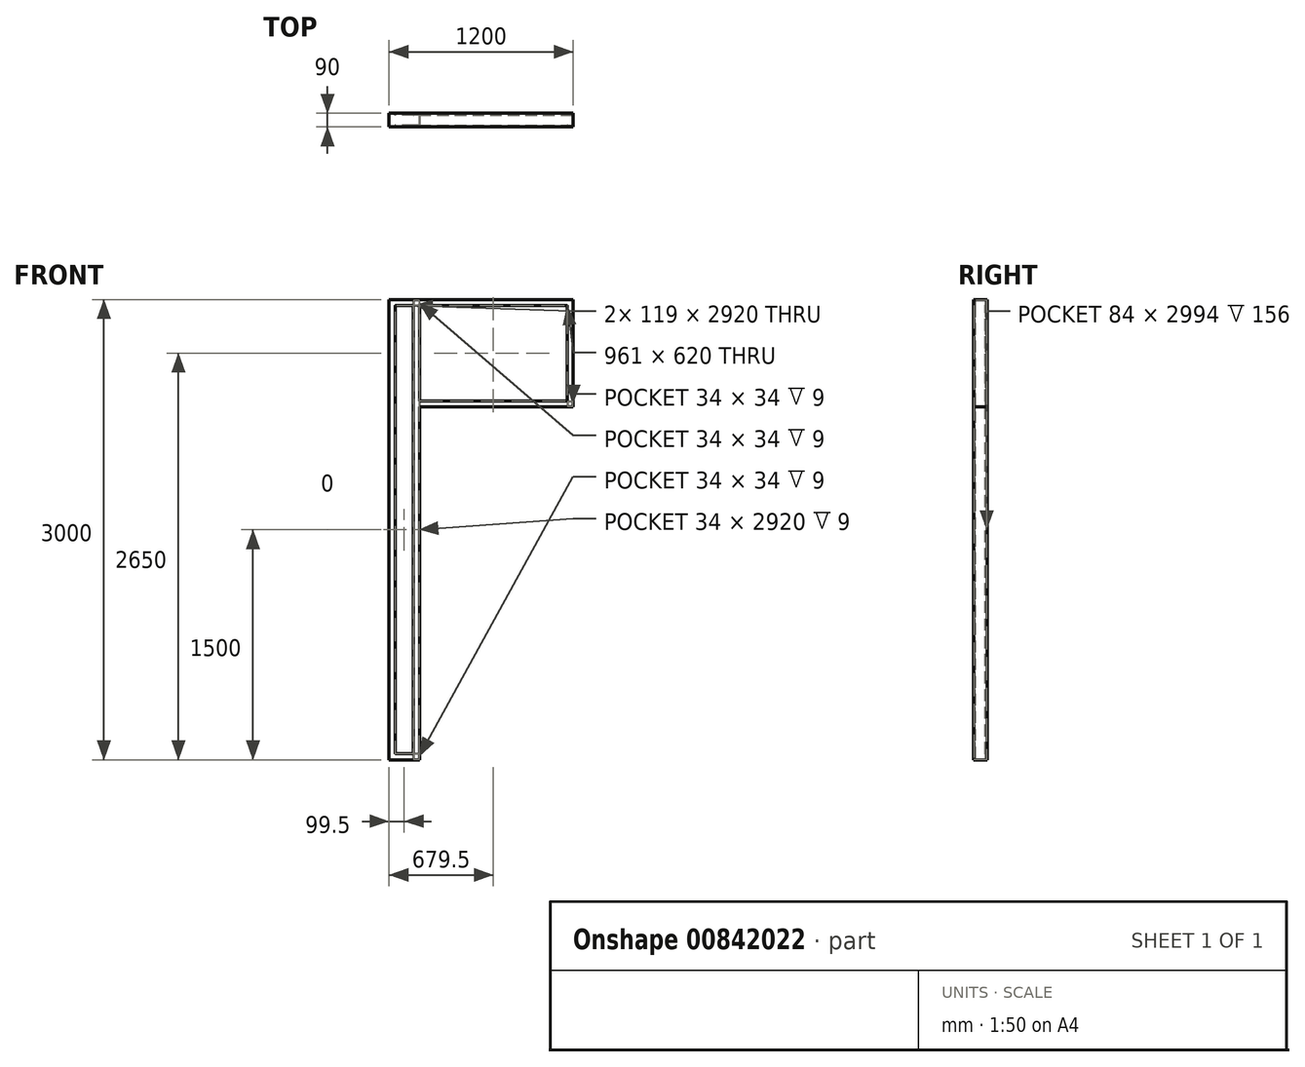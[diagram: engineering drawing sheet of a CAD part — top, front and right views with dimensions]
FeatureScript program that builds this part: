
annotation { "Feature Type Name" : "Feature", "Feature Type Description" : "" }
export const myFeature = defineFeature(function(context is Context, id is Id, definition is map)
    precondition{}
    {
        {
            var Q0;
            Q0=qCreatedBy(makeId("Front.planeOp"),FACE);
            var sketch = newSketch(context, id + "F0", { "sketchPlane" : qUnion([Q0])});
            skLineSegment(sketch, "E0.bottom", {"start": v(0, 0) * mm, "end": v(1200, 0) * mm});
            skLineSegment(sketch, "E0.top", {"start": v(0, 3000) * mm, "end": v(1200, 3000) * mm});
            skLineSegment(sketch, "E0.left", {"start": v(0, 0) * mm, "end": v(0, 3000) * mm});
            skLineSegment(sketch, "E0.right", {"start": v(1200, 0) * mm, "end": v(1200, 3000) * mm});
            skSolve(sketch);
        }
        {
            var Q0;
            Q0=qCreatedBy(makeId("Top.planeOp"),FACE);
            var sketch = newSketch(context, id + "F1", { "sketchPlane" : qUnion([Q0])});
            skLineSegment(sketch, "E1", {"start": v(0, 0) * mm, "end": v(0, -45) * mm});
            skLineSegment(sketch, "E2", {"start": v(0, -45) * mm, "end": v(40, -45) * mm});
            skLineSegment(sketch, "E3", {"start": v(40, -45) * mm, "end": v(40, -33) * mm});
            skLineSegment(sketch, "E4.MirrorCS", {"start": v(0, 0) * mm, "end": v(0, 45) * mm});
            skLineSegment(sketch, "E5.MirrorCS", {"start": v(0, 45) * mm, "end": v(40, 45) * mm});
            skLineSegment(sketch, "E6.MirrorCS", {"start": v(40, 45) * mm, "end": v(40, 33) * mm});
            skLineSegment(sketch, "E7.0", {"start": v(37, 42) * mm, "end": v(37, 33) * mm});
            skLineSegment(sketch, "E7.1", {"start": v(3, 42) * mm, "end": v(37, 42) * mm});
            skLineSegment(sketch, "E7.2", {"start": v(37, -42) * mm, "end": v(37, -33) * mm});
            skLineSegment(sketch, "E7.3", {"start": v(3, -42) * mm, "end": v(37, -42) * mm});
            skLineSegment(sketch, "E7.4", {"start": v(3, 0) * mm, "end": v(3, -42) * mm});
            skLineSegment(sketch, "E7.5", {"start": v(3, 0) * mm, "end": v(3, 42) * mm});
            skLineSegment(sketch, "E8", {"start": v(37, 33) * mm, "end": v(40, 33) * mm});
            skLineSegment(sketch, "E9", {"start": v(37, -33) * mm, "end": v(40, -33) * mm});
            skSolve(sketch);
        }
        {
            var Q0;
            Q0=qSketchRegion(id+"F1",true);
            var Q1;
            Q1=qConstructionFilter(qBodyType(qCreatedBy(id+"F0",EDGE),BodyType.WIRE),ConstructionObject.NO);
            sweep(context, id + "F2", {"profiles" : qUnion([Q0]), "path" : qUnion([Q1])});
        }
        {
            var Q0;
            Q0=qCreatedBy(makeId("Top.planeOp"),FACE);
            var sketch = newSketch(context, id + "F3", { "sketchPlane" : qUnion([Q0])});
            skLineSegment(sketch, "E10", {"start": v(159, -45) * mm, "end": v(199, -45) * mm});
            skLineSegment(sketch, "E11", {"start": v(199, -45) * mm, "end": v(199, 45) * mm});
            skLineSegment(sketch, "E12", {"start": v(199, 45) * mm, "end": v(159, 45) * mm});
            skLineSegment(sketch, "E13", {"start": v(159, 45) * mm, "end": v(159, 33) * mm});
            skLineSegment(sketch, "E14", {"start": v(159, -45) * mm, "end": v(159, -33) * mm});
            skLineSegment(sketch, "E15", {"start": v(200, -276.13) * mm, "end": v(200, 155.47) * mm, "construction": true});
            skLineSegment(sketch, "E16.0", {"start": v(1195, -40) * mm, "end": v(5, -40) * mm});
            skLineSegment(sketch, "E16.1", {"start": v(1195, 40) * mm, "end": v(1195, -40) * mm});
            skLineSegment(sketch, "E16.2", {"start": v(5, 40) * mm, "end": v(1195, 40) * mm});
            skLineSegment(sketch, "E16.3", {"start": v(5, 40) * mm, "end": v(5, -40) * mm});
            skLineSegment(sketch, "E17.0", {"start": v(162, 42) * mm, "end": v(162, 33) * mm});
            skLineSegment(sketch, "E17.1", {"start": v(162, -42) * mm, "end": v(162, -33) * mm});
            skLineSegment(sketch, "E17.2", {"start": v(162, -42) * mm, "end": v(196, -42) * mm});
            skLineSegment(sketch, "E17.3", {"start": v(196, -42) * mm, "end": v(196, 42) * mm});
            skLineSegment(sketch, "E17.4", {"start": v(196, 42) * mm, "end": v(162, 42) * mm});
            skLineSegment(sketch, "E18", {"start": v(162, -33) * mm, "end": v(159, -33) * mm});
            skLineSegment(sketch, "E19", {"start": v(162, 33) * mm, "end": v(159, 33) * mm});
            skSolve(sketch);
        }
        {
            var Q0;
            {var subQ1=sQuery(id+"F3.wireOp",EDGE,"E10");Q0=makeQuery(id+"F3.imprint","IMPRINT",FACE,{"disambiguationData":[TD([[makeQuery(id+"F3.imprint","IMPRINT",EDGE,{"derivedFrom":subQ1}),1.0]])]});}
            var Q1;
            {var subQ0=sQuery(id+"F3.wireOp",EDGE,"E16.0");var subQ1=sQuery(id+"F3.wireOp",EDGE,"E11");var subQ2=makeQuery(id+"F3.imprint","INTERSECT",VERTEX,{"derivedFrom":[subQ1,subQ0]});Q1=makeQuery(id+"F3.imprint","IMPRINT",FACE,{"disambiguationData":[TD([[makeQuery(id+"F3.imprint","IMPRINT",EDGE,{"disambiguationData":[TD([[subQ2,-1.0]])],"derivedFrom":subQ1}),1.0]])]});}
            var Q2;
            {var subQ0=sQuery(id+"F3.wireOp",EDGE,"E18");Q2=makeQuery(id+"F3.imprint","IMPRINT",FACE,{"disambiguationData":[TD([[makeQuery(id+"F3.imprint","IMPRINT",EDGE,{"derivedFrom":subQ0}),1.0]])]});}
            var Q3;
            {var subQ1=sQuery(id+"F3.wireOp",EDGE,"E12");Q3=makeQuery(id+"F3.imprint","IMPRINT",FACE,{"disambiguationData":[TD([[makeQuery(id+"F3.imprint","IMPRINT",EDGE,{"derivedFrom":subQ1}),1.0]])]});}
            var Q4;
            {var subQ0=sQuery(id+"F3.wireOp",EDGE,"E19");Q4=makeQuery(id+"F3.imprint","IMPRINT",FACE,{"disambiguationData":[TD([[makeQuery(id+"F3.imprint","IMPRINT",EDGE,{"derivedFrom":subQ0}),-1.0]])]});}
            var Q5;
            {var subQ0=sQuery(id+"F3.wireOp",EDGE,"fbeb7f0c-a459-400f-91ed-7fec257c8f050.MirrorCS");Q5=makeQuery(id+"F3.imprint","IMPRINT",FACE,{"disambiguationData":[TD([[makeQuery(id+"F3.imprint","IMPRINT",EDGE,{"derivedFrom":subQ0}),1.0]])]});}
            var Q6;
            {var subQ1=sQuery(id+"F3.wireOp",EDGE,"567eaf2c-da89-443f-b3b3-d68592a5250c0.MirrorCS");Q6=makeQuery(id+"F3.imprint","IMPRINT",FACE,{"disambiguationData":[TD([[makeQuery(id+"F3.imprint","IMPRINT",EDGE,{"derivedFrom":subQ1}),-1.0]])]});}
            var Q7;
            {var subQ0=sQuery(id+"F3.wireOp",EDGE,"E16.0");var subQ1=sQuery(id+"F3.wireOp",EDGE,"1e470031-5891-413e-a47c-f06d65b3e17f0.MirrorCS");var subQ2=makeQuery(id+"F3.imprint","INTERSECT",VERTEX,{"derivedFrom":[subQ1,subQ0]});Q7=makeQuery(id+"F3.imprint","IMPRINT",FACE,{"disambiguationData":[TD([[makeQuery(id+"F3.imprint","IMPRINT",EDGE,{"disambiguationData":[TD([[subQ2,-1.0]])],"derivedFrom":subQ1}),-1.0]])]});}
            var Q8;
            {var subQ5=sQuery(id+"F3.wireOp",EDGE,"ca9fbca5-8cf1-4a5b-8b27-837bc25230130.MirrorCS");Q8=makeQuery(id+"F3.imprint","IMPRINT",FACE,{"disambiguationData":[TD([[makeQuery(id+"F3.imprint","IMPRINT",EDGE,{"derivedFrom":subQ5}),-1.0]])]});}
            var Q9;
            {var subQ0=sQuery(id+"F3.wireOp",EDGE,"47aaed49-ff0d-4512-a623-d8c6419a6b470.MirrorCS");Q9=makeQuery(id+"F3.imprint","IMPRINT",FACE,{"disambiguationData":[TD([[makeQuery(id+"F3.imprint","IMPRINT",EDGE,{"derivedFrom":subQ0}),-1.0]])]});}
            var Q10;
            Q10=makeQuery(id+"F2.opSweep","SWEPT_FACE",FACE,{"disambiguationData":[OSD([sQuery(id+"F0.wireOp",EDGE,"E0.top"),sQuery(id+"F1.wireOp",EDGE,"E7.4"),sQuery(id+"F1.wireOp",EDGE,"E7.5")])]});
            extrude(context, id + "F4", {"entities" : qUnion([Q0, Q1, Q2, Q3, Q4, Q5, Q6, Q7, Q8, Q9]), "operationType" : NewBodyOperationType.ADD, "endBound" : BoundingType.UP_TO_SURFACE, "depth" : 25 * mm, "endBoundEntityFace" : qUnion([Q10]), "offsetDistance" : 25 * mm});
        }
        {
            var Q0;
            Q0=makeQuery(id+"F4.boolean.opBoolean","MERGE",FACE,{"derivedFrom":[makeQuery(id+"F2.opSweep","SWEPT_FACE",FACE,{"disambiguationData":[OSD([sQuery(id+"F0.wireOp",EDGE,"E0.left"),sQuery(id+"F1.wireOp",EDGE,"E2")])]}),makeQuery(id+"F4.opExtrude","SWEPT_FACE",FACE,{"disambiguationData":[OSD([sQuery(id+"F3.wireOp",EDGE,"E10")])]})]});
            var sketch = newSketch(context, id + "F5", { "sketchPlane" : qUnion([Q0])});
            skLineSegment(sketch, "E20.bottom", {"start": v(199, 0) * mm, "end": v(1200, 0) * mm});
            skLineSegment(sketch, "E20.top", {"start": v(199, 2300) * mm, "end": v(1200, 2300) * mm});
            skLineSegment(sketch, "E20.left", {"start": v(199, 0) * mm, "end": v(199, 2300) * mm});
            skLineSegment(sketch, "E20.right", {"start": v(1200, 0) * mm, "end": v(1200, 2300) * mm});
            skSolve(sketch);
        }
        {
            var Q0;
            Q0=qSketchRegion(id+"F5",true);
            extrude(context, id + "F6", {"entities" : qUnion([Q0]), "operationType" : NewBodyOperationType.REMOVE, "endBound" : BoundingType.THROUGH_ALL, "oppositeDirection" : true, "depth" : 25 * mm, "offsetDistance" : 25 * mm});
        }
        {
            var Q0;
            Q0=makeQuery(id+"F2.opSweep","SWEPT_FACE",FACE,{"disambiguationData":[OSD([sQuery(id+"F0.wireOp",EDGE,"E0.right"),sQuery(id+"F1.wireOp",EDGE,"E1"),sQuery(id+"F1.wireOp",EDGE,"E4.MirrorCS")])]});
            var sketch = newSketch(context, id + "F7", { "sketchPlane" : qUnion([Q0])});
            skLineSegment(sketch, "E21", {"start": v(-45, 2340) * mm, "end": v(-45, 2300) * mm});
            skLineSegment(sketch, "E22", {"start": v(-45, 2300) * mm, "end": v(45, 2300) * mm});
            skLineSegment(sketch, "E23", {"start": v(45, 2300) * mm, "end": v(45, 2340) * mm});
            skLineSegment(sketch, "E24", {"start": v(45, 2340) * mm, "end": v(33, 2340) * mm});
            skLineSegment(sketch, "E25", {"start": v(-45, 2340) * mm, "end": v(-33, 2340) * mm});
            skLineSegment(sketch, "E26.0", {"start": v(-42, 2337) * mm, "end": v(-33, 2337) * mm});
            skLineSegment(sketch, "E26.1", {"start": v(42, 2337) * mm, "end": v(33, 2337) * mm});
            skLineSegment(sketch, "E26.2", {"start": v(42, 2303) * mm, "end": v(42, 2337) * mm});
            skLineSegment(sketch, "E26.3", {"start": v(-42, 2303) * mm, "end": v(42, 2303) * mm});
            skLineSegment(sketch, "E26.4", {"start": v(-42, 2337) * mm, "end": v(-42, 2303) * mm});
            skLineSegment(sketch, "E27.0", {"start": v(-40, 2305) * mm, "end": v(40, 2305) * mm});
            skLineSegment(sketch, "E27.1", {"start": v(-40, 2995) * mm, "end": v(-40, 2305) * mm});
            skLineSegment(sketch, "E27.2", {"start": v(40, 2995) * mm, "end": v(-40, 2995) * mm});
            skLineSegment(sketch, "E27.3", {"start": v(40, 2305) * mm, "end": v(40, 2995) * mm});
            skLineSegment(sketch, "E28", {"start": v(-33, 2340) * mm, "end": v(-33, 2337) * mm});
            skLineSegment(sketch, "E29", {"start": v(33, 2340) * mm, "end": v(33, 2337) * mm});
            skSolve(sketch);
        }
        {
            var Q0;
            {var subQ9=sQuery(id+"F7.wireOp",EDGE,"E21");Q0=makeQuery(id+"F7.imprint","IMPRINT",FACE,{"disambiguationData":[TD([[makeQuery(id+"F7.imprint","IMPRINT",EDGE,{"derivedFrom":subQ9}),1.0]])]});}
            var Q1;
            {var subQ0=sQuery(id+"F7.wireOp",EDGE,"E29");Q1=makeQuery(id+"F7.imprint","IMPRINT",FACE,{"disambiguationData":[TD([[makeQuery(id+"F7.imprint","IMPRINT",EDGE,{"derivedFrom":subQ0}),1.0]])]});}
            var Q2;
            {var subQ0=sQuery(id+"F7.wireOp",EDGE,"E28");Q2=makeQuery(id+"F7.imprint","IMPRINT",FACE,{"disambiguationData":[TD([[makeQuery(id+"F7.imprint","IMPRINT",EDGE,{"derivedFrom":subQ0}),-1.0]])]});}
            var Q3;
            Q3=makeQuery(id+"F6.boolean.opBoolean","MERGE",FACE,{"derivedFrom":[makeQuery(id+"F4.opExtrude","SWEPT_FACE",FACE,{"disambiguationData":[OSD([sQuery(id+"F3.wireOp",EDGE,"E11")])]}),makeQuery(id+"F6.opExtrude","SWEPT_FACE",FACE,{"disambiguationData":[OSD([sQuery(id+"F5.wireOp",EDGE,"E20.left")])]})]});
            extrude(context, id + "F8", {"entities" : qUnion([Q0, Q1, Q2]), "operationType" : NewBodyOperationType.ADD, "endBound" : BoundingType.UP_TO_SURFACE, "oppositeDirection" : true, "depth" : 263 * mm, "endBoundEntityFace" : qUnion([Q3]), "offsetDistance" : 25 * mm});
        }
    });
